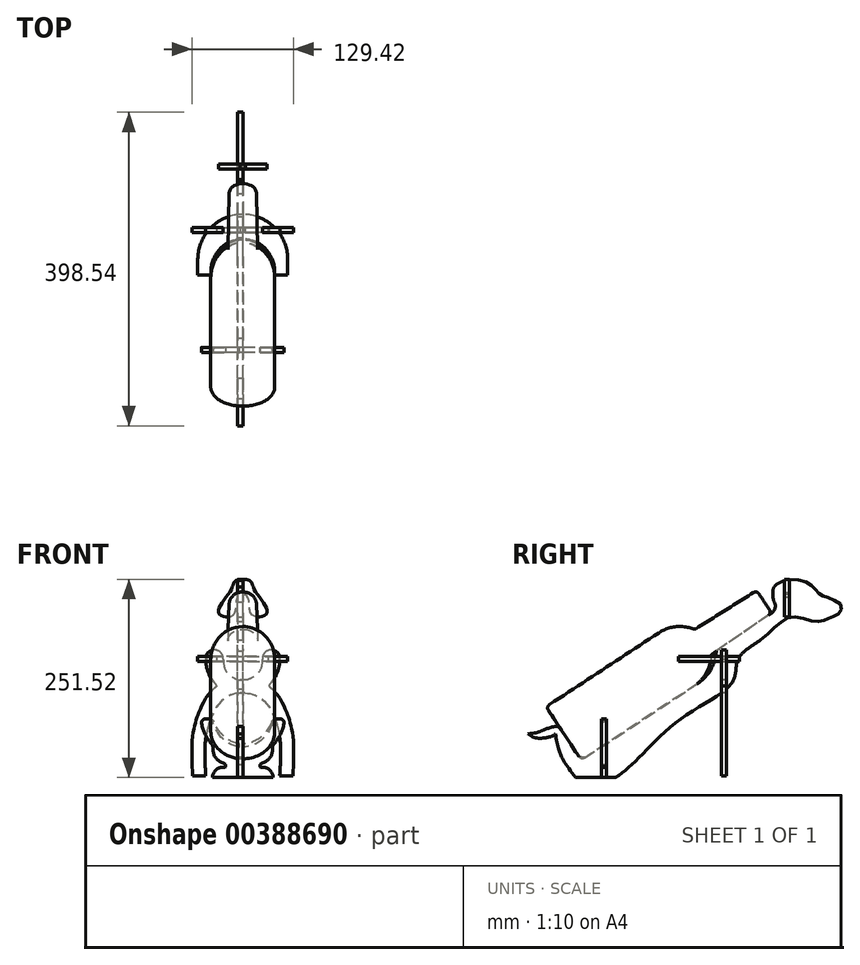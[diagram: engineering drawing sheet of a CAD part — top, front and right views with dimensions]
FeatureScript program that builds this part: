
annotation { "Feature Type Name" : "Feature", "Feature Type Description" : "" }
export const myFeature = defineFeature(function(context is Context, id is Id, definition is map)
    precondition{}
    {
        {
            var Q0;
            Q0=qCreatedBy(makeId("Right.planeOp"),FACE);
            var sketch = newSketch(context, id + "F0", { "sketchPlane" : qUnion([Q0])});
            skLineSegment(sketch, "E0", {"start": v(127.91, 114.02) * mm, "end": v(-126.79, -53.4) * mm});
            skLineSegment(sketch, "E1", {"start": v(-126.79, -53.4) * mm, "end": v(-107.26, -83.12) * mm});
            skLineSegment(sketch, "E2", {"start": v(16.48, 40.77) * mm, "end": v(38.8, 6.81) * mm, "construction": true});
            skLineSegment(sketch, "E3", {"start": v(50.09, 62.86) * mm, "end": v(60.55, 46.94) * mm, "construction": true});
            skLineSegment(sketch, "E4", {"start": v(127.91, 114.02) * mm, "end": v(134.6, 103.85) * mm});
            skLineSegment(sketch, "E5", {"start": v(38.8, 6.81) * mm, "end": v(-100.22, -84.57) * mm});
            skLineSegment(sketch, "E6", {"start": v(133.23, 96.87) * mm, "end": v(62.16, 48.05) * mm});
            skPoint(sketch, "E7.visualSharp", {"position": v(60.55, 46.94) * mm});
            skPoint(sketch, "E8.visualSharp", {"position": v(137.33, 99.7) * mm});
            skArc(sketch, "E8.filletArc", {"start": v(133.23, 96.87) * mm, "mid": v(135.34, 100.08) * mm, "end": v(134.6, 103.85) * mm});
            skPoint(sketch, "E9.visualSharp", {"position": v(-104.47, -87.36) * mm});
            skArc(sketch, "E9.filletArc", {"start": v(-107.26, -83.12) * mm, "mid": v(-104.04, -85.3) * mm, "end": v(-100.22, -84.57) * mm});
            skArc(sketch, "E10", {"start": v(38.8, 6.81) * mm, "mid": v(54.27, 23.32) * mm, "end": v(60.5, 45.07) * mm});
            skArc(sketch, "E11.filletArc", {"start": v(62.16, 48.05) * mm, "mid": v(60.98, 46.75) * mm, "end": v(60.5, 45.07) * mm});
            skSolve(sketch);
        }
        {
            var Q0;
            Q0=qCreatedBy(makeId("Right.planeOp"),FACE);
            var sketch = newSketch(context, id + "F1", { "sketchPlane" : qUnion([Q0])});
            skLineSegment(sketch, "E12", {"start": v(126.38, 106.7) * mm, "end": v(-128.33, -60.73) * mm});
            skLineSegment(sketch, "E13", {"start": v(-128.33, -60.73) * mm, "end": v(-108.8, -90.44) * mm});
            skLineSegment(sketch, "E14", {"start": v(14.94, 33.45) * mm, "end": v(37.27, -0.51) * mm, "construction": true});
            skLineSegment(sketch, "E15", {"start": v(48.55, 55.54) * mm, "end": v(59.01, 39.62) * mm, "construction": true});
            skLineSegment(sketch, "E16", {"start": v(126.38, 106.7) * mm, "end": v(133.06, 96.52) * mm});
            skLineSegment(sketch, "E17", {"start": v(37.27, -0.51) * mm, "end": v(-101.76, -91.9) * mm});
            skLineSegment(sketch, "E18", {"start": v(131.7, 89.55) * mm, "end": v(60.62, 40.72) * mm});
            skPoint(sketch, "E19.visualSharp", {"position": v(59.01, 39.62) * mm});
            skPoint(sketch, "E20.visualSharp", {"position": v(135.8, 92.37) * mm});
            skArc(sketch, "E20.filletArc", {"start": v(131.7, 89.55) * mm, "mid": v(133.8, 92.76) * mm, "end": v(133.06, 96.52) * mm});
            skPoint(sketch, "E21.visualSharp", {"position": v(-106, -94.69) * mm});
            skArc(sketch, "E21.filletArc", {"start": v(-108.8, -90.44) * mm, "mid": v(-105.58, -92.63) * mm, "end": v(-101.76, -91.9) * mm});
            skArc(sketch, "E22", {"start": v(37.27, -0.51) * mm, "mid": v(52.73, 16) * mm, "end": v(58.97, 37.74) * mm});
            skArc(sketch, "E23.filletArc", {"start": v(60.62, 40.72) * mm, "mid": v(59.44, 39.43) * mm, "end": v(58.97, 37.74) * mm});
            skLineSegment(sketch, "E24", {"start": v(150.96, 122.85) * mm, "end": v(-151.82, -76.17) * mm, "construction": true});
            skSolve(sketch);
        }
        {
            var Q0;
            Q0=makeQuery(id+"F1.imprint","IMPRINT",FACE,{"disambiguationData":[TD([[makeQuery(id+"F1.imprint","IMPRINT",EDGE,{"derivedFrom":sQuery(id+"F1.wireOp",EDGE,"E12")}),1.0]])]});
            var Q1;
            Q1=sQuery(id+"F1.wireOp",EDGE,"E24");
            revolve(context, id + "F2", {"entities" : qUnion([Q0]), "axis" : qUnion([Q1]), "revolveType" : RevolveType.FULL});
        }
        {
            var Q0;
            Q0=qCreatedBy(makeId("Right.planeOp"),FACE);
            cPlane(context, id + "F3", {"entities" : qUnion([Q0]), "cplaneType" : CPlaneType.OFFSET, "offset" : 1 / 203.2 * mm, "width" : 152.4 * mm, "height" : 152.4 * mm});
        }
        {
            var Q0;
            Q0=qCreatedBy(makeId("Right.planeOp"),FACE);
            var sketch = newSketch(context, id + "F4", { "sketchPlane" : qUnion([Q0])});
            skLineSegment(sketch, "E25", {"start": v(132.15, 111.22) * mm, "end": v(-122.55, -56.2) * mm});
            skLineSegment(sketch, "E26", {"start": v(-122.55, -56.2) * mm, "end": v(-103.02, -85.91) * mm});
            skLineSegment(sketch, "E27", {"start": v(20.72, 37.98) * mm, "end": v(43.04, 4.02) * mm, "construction": true});
            skLineSegment(sketch, "E28", {"start": v(54.33, 60.07) * mm, "end": v(64.8, 44.15) * mm, "construction": true});
            skLineSegment(sketch, "E29", {"start": v(132.15, 111.22) * mm, "end": v(138.84, 101.06) * mm});
            skLineSegment(sketch, "E30", {"start": v(43.04, 4.02) * mm, "end": v(-95.98, -87.37) * mm});
            skLineSegment(sketch, "E31", {"start": v(137.47, 94.08) * mm, "end": v(66.4, 45.25) * mm});
            skPoint(sketch, "E32.visualSharp", {"position": v(64.8, 44.15) * mm});
            skPoint(sketch, "E33.visualSharp", {"position": v(141.57, 96.9) * mm});
            skArc(sketch, "E33.filletArc", {"start": v(137.47, 94.08) * mm, "mid": v(139.58, 97.29) * mm, "end": v(138.84, 101.06) * mm});
            skPoint(sketch, "E34.visualSharp", {"position": v(-100.23, -90.16) * mm});
            skArc(sketch, "E34.filletArc", {"start": v(-103.02, -85.91) * mm, "mid": v(-99.8, -88.1) * mm, "end": v(-95.98, -87.37) * mm});
            skArc(sketch, "E35", {"start": v(43.04, 4.02) * mm, "mid": v(58.5, 20.53) * mm, "end": v(64.75, 42.27) * mm});
            skArc(sketch, "E36.filletArc", {"start": v(66.4, 45.25) * mm, "mid": v(65.22, 43.96) * mm, "end": v(64.75, 42.27) * mm});
            skLineSegment(sketch, "E37", {"start": v(156.74, 127.39) * mm, "end": v(-146.04, -71.64) * mm, "construction": true});
            skSolve(sketch);
        }
        {
            var Q0;
            Q0=qCreatedBy(id+"F3.planeOp",FACE);
            var sketch = newSketch(context, id + "F5", { "sketchPlane" : qUnion([Q0])});
            skLineSegment(sketch, "E38", {"start": v(129.3, 111.9) * mm, "end": v(-125.4, -55.52) * mm, "construction": true});
            skLineSegment(sketch, "E39", {"start": v(-125.4, -55.52) * mm, "end": v(-107.26, -83.12) * mm, "construction": true});
            skLineSegment(sketch, "E40", {"start": v(17.87, 38.65) * mm, "end": v(38.8, 6.82) * mm, "construction": true});
            skLineSegment(sketch, "E41", {"start": v(51.48, 60.74) * mm, "end": v(60.55, 46.95) * mm, "construction": true});
            skLineSegment(sketch, "E42", {"start": v(129.3, 111.9) * mm, "end": v(134.6, 103.86) * mm, "construction": true});
            skLineSegment(sketch, "E43", {"start": v(38.8, 6.82) * mm, "end": v(-100.22, -84.57) * mm, "construction": true});
            skLineSegment(sketch, "E44", {"start": v(133.23, 96.88) * mm, "end": v(62.15, 48.05) * mm, "construction": true});
            skPoint(sketch, "E45.visualSharp", {"position": v(60.55, 46.95) * mm});
            skPoint(sketch, "E46.visualSharp", {"position": v(137.33, 99.7) * mm});
            skArc(sketch, "E46.filletArc", {"start": v(133.23, 96.88) * mm, "mid": v(135.33, 100.09) * mm, "end": v(134.6, 103.86) * mm, "construction": true});
            skPoint(sketch, "E47.visualSharp", {"position": v(-104.47, -87.36) * mm});
            skArc(sketch, "E47.filletArc", {"start": v(-107.26, -83.12) * mm, "mid": v(-104.04, -85.3) * mm, "end": v(-100.22, -84.57) * mm, "construction": true});
            skArc(sketch, "E48", {"start": v(38.8, 6.82) * mm, "mid": v(54.27, 23.33) * mm, "end": v(60.5, 45.07) * mm, "construction": true});
            skArc(sketch, "E49.filletArc", {"start": v(62.15, 48.05) * mm, "mid": v(60.98, 46.76) * mm, "end": v(60.5, 45.07) * mm, "construction": true});
            skLineSegment(sketch, "E50.0", {"start": v(138.84, 106.65) * mm, "end": v(139.13, 106.2) * mm});
            skArc(sketch, "E50.1", {"start": v(136.1, 92.7) * mm, "mid": v(140.32, 99.11) * mm, "end": v(138.84, 106.65) * mm});
            skLineSegment(sketch, "E50.2", {"start": v(136.1, 92.7) * mm, "end": v(65.55, 44.22) * mm});
            skLineSegment(sketch, "E50.3", {"start": v(-129.48, -58.56) * mm, "end": v(-111.5, -85.9) * mm});
            skArc(sketch, "E50.4", {"start": v(-111.5, -85.9) * mm, "mid": v(-105.07, -90.28) * mm, "end": v(-97.43, -88.82) * mm});
            skLineSegment(sketch, "E50.5", {"start": v(41.6, 2.57) * mm, "end": v(-97.43, -88.82) * mm});
            skArc(sketch, "E50.6", {"start": v(41.6, 2.57) * mm, "mid": v(58.53, 20.54) * mm, "end": v(65.55, 44.22) * mm});
            skLineSegment(sketch, "E51", {"start": v(-113.23, -116.39) * mm, "end": v(-62.43, -116.39) * mm});
            skLineSegment(sketch, "E52", {"start": v(11, -17.54) * mm, "end": v(24.95, -38.77) * mm, "construction": true});
            skLineSegment(sketch, "E53", {"start": v(58.53, 20.54) * mm, "end": v(86.35, 5.26) * mm, "construction": true});
            skLineSegment(sketch, "E54", {"start": v(109.97, 74.74) * mm, "end": v(121.48, 57.99) * mm, "construction": true});
            skFitSpline(sketch, "E55", {"points": [v(-62.43, -116.39) * mm, v(-33.54, -92.29) * mm, v(24.95, -38.77) * mm, v(86.35, 5.26) * mm, v(93.72, 34.9) * mm, v(121.48, 57.99) * mm], "startDerivative": vector(159.16, 104.1) * mm, "endDerivative": vector(168.13, 123.76) * mm});
            skFitSpline(sketch, "E56", {"points": [v(121.48, 57.99) * mm, v(144.71, 78.58) * mm, v(164.56, 87.66) * mm, v(189.26, 81.98) * mm, v(202.82, 83.08) * mm, v(211.13, 87.06) * mm, v(220.95, 91.79) * mm, v(224.26, 101.6) * mm, v(210.78, 110.76) * mm, v(200, 114.83) * mm, v(193.5, 120.19) * mm, v(185.37, 128.25) * mm, v(165.8, 135.1) * mm, v(139.13, 125.69) * mm], "startDerivative": vector(256.26, 194.91) * mm, "endDerivative": vector(-141.62, -197.05) * mm});
            skLineSegment(sketch, "E57", {"start": v(-120.57, -72.1) * mm, "end": v(-134.37, -81.18) * mm, "construction": true});
            skFitSpline(sketch, "E58", {"points": [v(-113.23, -116.39) * mm, v(-130.64, -91.32) * mm, v(-134.37, -81.18) * mm, v(-138.76, -60.93) * mm], "startDerivative": vector(-50.46, 62) * mm, "endDerivative": vector(-7.82, 62.45) * mm});
            skFitSpline(sketch, "E59", {"points": [v(-138.76, -60.93) * mm, v(-147.9, -65.45) * mm, v(-173.85, -60.93) * mm], "startDerivative": vector(-24.4, -25.88) * mm, "endDerivative": vector(-40.71, 38.74) * mm});
            skFitSpline(sketch, "E60", {"points": [v(-173.85, -60.93) * mm, v(-153.82, -56.03) * mm, v(-135.34, -51.57) * mm], "startDerivative": vector(89.48, 8.4) * mm, "endDerivative": vector(32.86, -1.06) * mm});
            skLineSegment(sketch, "E61", {"start": v(-133.74, -53.46) * mm, "end": v(-129.84, -58.08) * mm});
            skArc(sketch, "E62.filletArc", {"start": v(-133.74, -53.46) * mm, "mid": v(-135.72, -52.03) * mm, "end": v(-138.13, -51.69) * mm});
            skPoint(sketch, "E63.visualSharp", {"position": v(-129.64, -58.3) * mm});
            skArc(sketch, "E63.filletArc", {"start": v(-129.48, -58.56) * mm, "mid": v(-129.65, -58.31) * mm, "end": v(-129.84, -58.08) * mm});
            skFitSpline(sketch, "E64", {"points": [v(139.13, 125.69) * mm, v(139.13, 106.2) * mm], "startDerivative": vector(-7.3, -7.68) * mm, "endDerivative": vector(7.6, -15.97) * mm});
            skSolve(sketch);
        }
        {
            var Q0;
            Q0 = qSketchRegion(id + "F5", true);
            extrude(context, id + "F6", {"entities" : qUnion([Q0]), "oppositeDirection" : true, "depth" : 6.35 * mm});
        }
        {
            var Q0;
            Q0=makeQuery(id+"F6.opExtrude","CAP_FACE",FACE,{"disambiguationData":[OSD([sQuery(id+"F5.wireOp",EDGE,"E50.0"),sQuery(id+"F5.wireOp",EDGE,"E50.1"),sQuery(id+"F5.wireOp",EDGE,"E50.2"),sQuery(id+"F5.wireOp",EDGE,"E50.3"),sQuery(id+"F5.wireOp",EDGE,"E50.4"),sQuery(id+"F5.wireOp",EDGE,"E50.5"),sQuery(id+"F5.wireOp",EDGE,"E50.6"),sQuery(id+"F5.wireOp",EDGE,"E51"),sQuery(id+"F5.wireOp",EDGE,"E55"),sQuery(id+"F5.wireOp",EDGE,"E56"),sQuery(id+"F5.wireOp",EDGE,"E58"),sQuery(id+"F5.wireOp",EDGE,"E59"),sQuery(id+"F5.wireOp",EDGE,"E60"),sQuery(id+"F5.wireOp",EDGE,"E61"),sQuery(id+"F5.wireOp",EDGE,"E62.filletArc"),sQuery(id+"F5.wireOp",EDGE,"E63.filletArc"),sQuery(id+"F5.wireOp",EDGE,"E64")])],"isStart":true});
            var sketch = newSketch(context, id + "F7", { "sketchPlane" : qUnion([Q0])});
            skLineSegment(sketch, "E65.bottom", {"start": v(158.54, 134.8) * mm, "end": v(152.2, 134.8) * mm});
            skLineSegment(sketch, "E65.top", {"start": v(158.54, 118.28) * mm, "end": v(152.2, 118.28) * mm});
            skLineSegment(sketch, "E65.left", {"start": v(158.54, 134.8) * mm, "end": v(158.54, 118.28) * mm});
            skLineSegment(sketch, "E65.right", {"start": v(152.2, 134.8) * mm, "end": v(152.2, 118.28) * mm});
            skLineSegment(sketch, "E66.bottom", {"start": v(71.86, -9.33) * mm, "end": v(78.21, -9.33) * mm});
            skLineSegment(sketch, "E66.top", {"start": v(71.86, 7.18) * mm, "end": v(78.21, 7.18) * mm});
            skLineSegment(sketch, "E66.left", {"start": v(71.86, -9.33) * mm, "end": v(71.86, 7.18) * mm});
            skLineSegment(sketch, "E66.right", {"start": v(78.21, -9.33) * mm, "end": v(78.21, 7.18) * mm});
            skLineSegment(sketch, "E67.bottom", {"start": v(94.97, 37) * mm, "end": v(78.46, 37) * mm});
            skLineSegment(sketch, "E67.top", {"start": v(94.97, 30.65) * mm, "end": v(78.46, 30.65) * mm});
            skLineSegment(sketch, "E67.left", {"start": v(94.97, 37) * mm, "end": v(94.97, 30.65) * mm});
            skLineSegment(sketch, "E67.right", {"start": v(78.46, 37) * mm, "end": v(78.46, 30.65) * mm});
            skLineSegment(sketch, "E68.bottom", {"start": v(-74.18, -116.39) * mm, "end": v(-80.53, -116.39) * mm});
            skLineSegment(sketch, "E68.top", {"start": v(-74.18, -99.88) * mm, "end": v(-80.53, -99.88) * mm});
            skLineSegment(sketch, "E68.left", {"start": v(-74.18, -116.39) * mm, "end": v(-74.18, -99.88) * mm});
            skLineSegment(sketch, "E68.right", {"start": v(-80.53, -116.39) * mm, "end": v(-80.53, -99.88) * mm});
            skSolve(sketch);
        }
        {
            var Q0;
            Q0 = qSketchRegion(id + "F7", true);
            extrude(context, id + "F8", {"entities" : qUnion([Q0]), "operationType" : NewBodyOperationType.REMOVE, "endBound" : BoundingType.UP_TO_NEXT, "oppositeDirection" : true, "depth" : 25.4 * mm});
        }
        {
            var Q0;
            Q0=makeQuery(id+"F8.boolean.opBoolean","COPY",FACE,{"derivedFrom":makeQuery(id+"F8.opExtrude","SWEPT_FACE",FACE,{"disambiguationData":[OSD([sQuery(id+"F7.wireOp",EDGE,"E68.right")])]})});
            cPlane(context, id + "F9", {"entities" : qUnion([Q0]), "cplaneType" : CPlaneType.OFFSET, "offset" : 0 * mm, "width" : 152.4 * mm, "height" : 152.4 * mm});
        }
        {
            var Q0;
            Q0=qCreatedBy(id+"F9.planeOp",FACE);
            var sketch = newSketch(context, id + "F10", { "sketchPlane" : qUnion([Q0])});
            skLineSegment(sketch, "E69", {"start": v(0, -40.19) * mm, "end": v(0, -116.39) * mm, "construction": true});
            skLineSegment(sketch, "E70", {"start": v(0, -76.17) * mm, "end": v(38.1, -76.17) * mm, "construction": true});
            skArc(sketch, "E71.0", {"start": v(39.63, -73.76) * mm, "mid": v(47.76, -61.8) * mm, "end": v(52.39, -48.11) * mm});
            skFitSpline(sketch, "E72", {"points": [v(38.45, -116.39) * mm, v(28.54, -104) * mm, v(21.75, -102.5) * mm], "startDerivative": vector(1.02, 30.03) * mm, "endDerivative": vector(-6.25, 15.83) * mm});
            skFitSpline(sketch, "E73", {"points": [v(21.75, -102.5) * mm, v(28.95, -96.1) * mm, v(36.72, -87.28) * mm, v(38.1, -75.4) * mm], "startDerivative": vector(-7.38, 35.84) * mm, "endDerivative": vector(2.11, 45.83) * mm});
            skArc(sketch, "E74.filletArc", {"start": v(39.63, -73.76) * mm, "mid": v(38.46, -75.63) * mm, "end": v(38, -77.79) * mm});
            skFitSpline(sketch, "E75.MirrorCS", {"points": [v(-38.45, -116.39) * mm, v(-28.54, -104) * mm, v(-21.75, -102.5) * mm], "startDerivative": vector(-1.02, 30.03) * mm, "endDerivative": vector(6.25, 15.83) * mm});
            skFitSpline(sketch, "E76.MirrorCS", {"points": [v(-21.75, -102.5) * mm, v(-28.95, -96.1) * mm, v(-36.72, -87.28) * mm, v(-38.1, -75.4) * mm], "startDerivative": vector(7.38, 35.84) * mm, "endDerivative": vector(-2.11, 45.83) * mm});
            skArc(sketch, "E77.MirrorCS", {"start": v(-39.63, -73.76) * mm, "mid": v(-47.76, -61.8) * mm, "end": v(-52.39, -48.11) * mm});
            skArc(sketch, "E78.MirrorCS", {"start": v(-39.63, -73.76) * mm, "mid": v(-38.46, -75.63) * mm, "end": v(-38, -77.79) * mm});
            skLineSegment(sketch, "E79.MirrorCS", {"start": v(0, -76.17) * mm, "end": v(-38.1, -76.17) * mm, "construction": true});
            skLineSegment(sketch, "E80", {"start": v(47.4, -42.07) * mm, "end": v(0, -42.07) * mm});
            skPoint(sketch, "E81.visualSharp", {"position": v(53.19, -42.07) * mm});
            skArc(sketch, "E81.filletArc", {"start": v(52.39, -48.11) * mm, "mid": v(51.31, -43.92) * mm, "end": v(47.4, -42.07) * mm});
            skPoint(sketch, "E82.MirrorP", {"position": v(-53.19, -42.07) * mm});
            skLineSegment(sketch, "E83.MirrorCS", {"start": v(-47.4, -42.07) * mm, "end": v(0, -42.07) * mm});
            skArc(sketch, "E84.MirrorCS", {"start": v(-52.39, -48.11) * mm, "mid": v(-51.31, -43.92) * mm, "end": v(-47.4, -42.07) * mm});
            skPoint(sketch, "E85.MirrorCS.start.orphan", {"position": v(-39.63, -73.76) * mm});
            skLineSegment(sketch, "E86", {"start": v(0, -116.39) * mm, "end": v(38.45, -116.39) * mm});
            skLineSegment(sketch, "E87.MirrorCS", {"start": v(0, -116.39) * mm, "end": v(-38.45, -116.39) * mm});
            skSolve(sketch);
        }
        {
            var Q0;
            Q0 = qSketchRegion(id + "F10", true);
            extrude(context, id + "F11", {"entities" : qUnion([Q0]), "depth" : 6.35 * mm});
        }
        {
            var Q0;
            Q0=makeQuery(id+"F8.boolean.opBoolean","COPY",FACE,{"derivedFrom":makeQuery(id+"F8.opExtrude","SWEPT_FACE",FACE,{"disambiguationData":[OSD([sQuery(id+"F7.wireOp",EDGE,"E67.top")])]})});
            var sketch = newSketch(context, id + "F12", { "sketchPlane" : qUnion([Q0])});
            skLineSegment(sketch, "E88", {"start": v(0, 92.08) * mm, "end": v(0, 60.86) * mm, "construction": true});
            skPoint(sketch, "E88.endSnap0", {"position": v(0, 78.46) * mm});
            skLineSegment(sketch, "E89", {"start": v(0, 37.82) * mm, "end": v(0, 94.97) * mm, "construction": true});
            skLineSegment(sketch, "E90", {"start": v(0, 60.86) * mm, "end": v(-16.24, 60.86) * mm, "construction": true});
            skLineSegment(sketch, "E91", {"start": v(0, 37.82) * mm, "end": v(-40.64, 37.82) * mm, "construction": true});
            skArc(sketch, "E92", {"start": v(0, 78.46) * mm, "mid": v(-28.74, 66.55) * mm, "end": v(-40.64, 37.82) * mm, "construction": true});
            skArc(sketch, "E93.0", {"start": v(0, 94.97) * mm, "mid": v(-40.41, 78.23) * mm, "end": v(-57.15, 37.82) * mm});
            skLineSegment(sketch, "E94", {"start": v(-40.64, 37.82) * mm, "end": v(-57.15, 37.82) * mm, "construction": true});
            skPoint(sketch, "E95.start.orphan", {"position": v(0, 105.65) * mm});
            skLineSegment(sketch, "E96.MirrorCS", {"start": v(0, 60.86) * mm, "end": v(16.24, 60.86) * mm, "construction": true});
            skLineSegment(sketch, "E97.MirrorCS", {"start": v(0, 37.82) * mm, "end": v(40.64, 37.82) * mm, "construction": true});
            skLineSegment(sketch, "E98.MirrorCS", {"start": v(40.64, 37.82) * mm, "end": v(57.15, 37.82) * mm, "construction": true});
            skArc(sketch, "E99.MirrorCS", {"start": v(0, 78.46) * mm, "mid": v(28.74, 66.55) * mm, "end": v(40.64, 37.82) * mm, "construction": true});
            skArc(sketch, "E100.MirrorCS", {"start": v(0, 94.97) * mm, "mid": v(40.41, 78.23) * mm, "end": v(57.15, 37.82) * mm});
            skLineSegment(sketch, "E101", {"start": v(57.15, 37.82) * mm, "end": v(57.15, 17.76) * mm});
            skLineSegment(sketch, "E102", {"start": v(40.64, 17.76) * mm, "end": v(40.64, 37.82) * mm, "construction": true});
            skLineSegment(sketch, "E103.MirrorCS", {"start": v(-57.15, 37.82) * mm, "end": v(-57.15, 17.76) * mm});
            skLineSegment(sketch, "E104.MirrorCS", {"start": v(-40.64, 17.76) * mm, "end": v(-40.64, 37.82) * mm, "construction": true});
            skLineSegment(sketch, "E105", {"start": v(57.15, 17.76) * mm, "end": v(-57.15, 17.76) * mm});
            skSolve(sketch);
        }
        {
            var Q0;
            Q0 = qSketchRegion(id + "F12", true);
            extrude(context, id + "F13", {"entities" : qUnion([Q0]), "depth" : 6.35 * mm});
        }
        {
            var Q0;
            Q0=makeQuery(id+"F8.boolean.opBoolean","COPY",FACE,{"derivedFrom":makeQuery(id+"F8.opExtrude","SWEPT_FACE",FACE,{"disambiguationData":[OSD([sQuery(id+"F7.wireOp",EDGE,"E66.left")])]})});
            var sketch = newSketch(context, id + "F14", { "sketchPlane" : qUnion([Q0])});
            skLineSegment(sketch, "E106", {"start": v(0, -9.33) * mm, "end": v(38.1, -9.33) * mm, "construction": true});
            skLineSegment(sketch, "E107", {"start": v(0, -9.33) * mm, "end": v(0, 49.4) * mm, "construction": true});
            skPoint(sketch, "E107.endSnap0", {"position": v(0, 7.18) * mm});
            skLineSegment(sketch, "E108", {"start": v(0, 28.02) * mm, "end": v(38.1, 28.02) * mm, "construction": true});
            skLineSegment(sketch, "E109", {"start": v(0, 34.37) * mm, "end": v(38.1, 34.37) * mm, "construction": true});
            skLineSegment(sketch, "E110", {"start": v(0, -114.37) * mm, "end": v(-47, -114.37) * mm, "construction": true});
            skFitSpline(sketch, "E111", {"points": [v(-3.17, -9.33) * mm, v(-40.9, -42.11) * mm, v(-47, -114.37) * mm], "startDerivative": vector(-141.52, -3.48) * mm, "endDerivative": vector(12.9, -201.55) * mm});
            skLineSegment(sketch, "E112", {"start": v(-3.17, -9.33) * mm, "end": v(0, -9.33) * mm});
            skArc(sketch, "E113", {"start": v(-47.2, 34.37) * mm, "mid": v(-43.8, 16.78) * mm, "end": v(-34.1, 1.72) * mm});
            skFitSpline(sketch, "E114", {"points": [v(-24.85, 34.37) * mm, v(-18.77, 15.57) * mm, v(-3.18, 7.18) * mm], "startDerivative": vector(2.66, -57.69) * mm, "endDerivative": vector(26.33, 0.45) * mm});
            skFitSpline(sketch, "E115.0", {"points": [v(-3.7, 9.85) * mm, v(-5.78, 9.79) * mm, v(-9.9, 9.42) * mm, v(-15.79, 8.2) * mm, v(-21.34, 6.3) * mm, v(-26.48, 3.85) * mm, v(-31.16, 0.92) * mm, v(-35.37, -2.38) * mm, v(-39.12, -5.97) * mm, v(-43.55, -11) * mm, v(-48.11, -17.62) * mm, v(-51.68, -24.32) * mm, v(-53.77, -28.94) * mm, v(-54.87, -31.55) * mm, v(-55.64, -33.47) * mm, v(-56.25, -35.06) * mm, v(-56.71, -36.3) * mm, v(-57.4, -38.18) * mm, v(-58.37, -41) * mm, v(-59.54, -44.8) * mm, v(-60.6, -48.63) * mm, v(-61.52, -52.52) * mm, v(-62.6, -57.79) * mm, v(-63.61, -64.57) * mm, v(-64.36, -73.13) * mm, v(-64.68, -82.26) * mm, v(-64.6, -95.46) * mm, v(-64.03, -106.84) * mm, v(-63.46, -115.4) * mm]});
            skLineSegment(sketch, "E116", {"start": v(-47, -114.37) * mm, "end": v(-63.53, -114.37) * mm});
            skLineSegment(sketch, "E117", {"start": v(-47.2, 34.37) * mm, "end": v(-24.85, 34.37) * mm, "construction": true});
            skLineSegment(sketch, "E118", {"start": v(-3.18, 7.18) * mm, "end": v(0, 7.18) * mm});
            skArc(sketch, "E119", {"start": v(-24.85, 34.37) * mm, "mid": v(-36.03, 45.54) * mm, "end": v(-47.2, 34.37) * mm});
            skPoint(sketch, "E120.visualSharp", {"position": v(-30.92, -1.3) * mm});
            skArc(sketch, "E120.filletArc", {"start": v(-34.47, -3.9) * mm, "mid": v(-33.04, -1.17) * mm, "end": v(-34.1, 1.72) * mm});
            skFitSpline(sketch, "E121.MirrorCS", {"points": [v(3.17, -9.33) * mm, v(40.9, -42.11) * mm, v(47, -114.37) * mm], "startDerivative": vector(141.52, -3.48) * mm, "endDerivative": vector(-12.9, -201.55) * mm});
            skArc(sketch, "E122.MirrorCS", {"start": v(47.2, 34.37) * mm, "mid": v(43.8, 16.78) * mm, "end": v(34.1, 1.72) * mm});
            skArc(sketch, "E123.MirrorCS", {"start": v(24.85, 34.37) * mm, "mid": v(36.03, 45.54) * mm, "end": v(47.2, 34.37) * mm});
            skFitSpline(sketch, "E124.MirrorCS", {"points": [v(24.85, 34.37) * mm, v(18.77, 15.57) * mm, v(3.17, 7.18) * mm], "startDerivative": vector(-2.66, -57.69) * mm, "endDerivative": vector(-26.33, 0.45) * mm});
            skLineSegment(sketch, "E125.MirrorCS", {"start": v(47, -114.37) * mm, "end": v(63.53, -114.37) * mm});
            skLineSegment(sketch, "E126.MirrorCS", {"start": v(3.17, -9.33) * mm, "end": v(0, -9.33) * mm});
            skLineSegment(sketch, "E127.MirrorCS", {"start": v(3.18, 7.18) * mm, "end": v(0, 7.18) * mm});
            skPoint(sketch, "E128.MirrorP", {"position": v(30.92, -1.3) * mm});
            skArc(sketch, "E129.MirrorCS", {"start": v(34.47, -3.9) * mm, "mid": v(33.04, -1.17) * mm, "end": v(34.1, 1.72) * mm});
            skFitSpline(sketch, "E130.trimOffspring", {"points": [v(3.7, 9.85) * mm, v(5.78, 9.79) * mm, v(9.9, 9.42) * mm, v(15.79, 8.2) * mm, v(21.34, 6.3) * mm, v(26.48, 3.85) * mm, v(31.16, 0.92) * mm, v(35.37, -2.38) * mm, v(39.12, -5.97) * mm, v(43.55, -11) * mm, v(48.11, -17.62) * mm, v(51.68, -24.32) * mm, v(53.77, -28.94) * mm, v(54.87, -31.55) * mm, v(55.64, -33.47) * mm, v(56.25, -35.06) * mm, v(56.71, -36.3) * mm, v(57.4, -38.18) * mm, v(58.37, -41) * mm, v(59.54, -44.8) * mm, v(60.6, -48.63) * mm, v(61.52, -52.52) * mm, v(62.6, -57.79) * mm, v(63.61, -64.57) * mm, v(64.36, -73.13) * mm, v(64.68, -82.26) * mm, v(64.6, -95.46) * mm, v(64.03, -106.84) * mm, v(63.46, -115.4) * mm]});
            skSolve(sketch);
        }
        {
            var Q0;
            Q0 = qSketchRegion(id + "F14", true);
            var Q1;
            Q1=makeQuery(id+"F14.imprint","IMPRINT",FACE,{"disambiguationData":[TD([[makeQuery(id+"F14.imprint","IMPRINT",EDGE,{"derivedFrom":sQuery(id+"F14.wireOp",EDGE,"E111")}),-1.0]])]});
            extrude(context, id + "F15", {"entities" : qUnion([Q0, Q1]), "depth" : 6.35 * mm});
        }
        {
            var Q0;
            Q0=makeQuery(id+"F8.boolean.opBoolean","COPY",FACE,{"derivedFrom":makeQuery(id+"F8.opExtrude","SWEPT_FACE",FACE,{"disambiguationData":[OSD([sQuery(id+"F7.wireOp",EDGE,"E65.right")])]})});
            var sketch = newSketch(context, id + "F16", { "sketchPlane" : qUnion([Q0])});
            skFitSpline(sketch, "E131", {"points": [v(-3.2, 135.14) * mm, v(-9.9, 132.96) * mm, v(-15.3, 121.2) * mm, v(-30.6, 92.3) * mm, v(-12.46, 89.5) * mm, v(-7.85, 107.31) * mm, v(-3.43, 116.08) * mm], "startDerivative": vector(-41.32, -0.75) * mm, "endDerivative": vector(28.6, 19.54) * mm});
            skLineSegment(sketch, "E132", {"start": v(0, 135.13) * mm, "end": v(-3.43, 135.13) * mm});
            skLineSegment(sketch, "E133", {"start": v(0, 116.08) * mm, "end": v(-3.43, 116.08) * mm});
            skLineSegment(sketch, "E134", {"start": v(0, 116.08) * mm, "end": v(0, 135.13) * mm, "construction": true});
            skLineSegment(sketch, "E135.MirrorCS", {"start": v(0, 116.08) * mm, "end": v(3.43, 116.08) * mm});
            skFitSpline(sketch, "E136.MirrorCS", {"points": [v(3.2, 135.14) * mm, v(9.9, 132.96) * mm, v(15.3, 121.2) * mm, v(30.6, 92.3) * mm, v(12.46, 89.5) * mm, v(7.85, 107.31) * mm, v(3.43, 116.08) * mm], "startDerivative": vector(41.32, -0.75) * mm, "endDerivative": vector(-28.6, 19.54) * mm});
            skLineSegment(sketch, "E137.MirrorCS", {"start": v(0, 135.13) * mm, "end": v(3.43, 135.13) * mm});
            skSolve(sketch);
        }
        {
            var Q0;
            Q0=makeQuery(id+"F2.opRevolve","SWEPT_BODY",BODY,{"disambiguationData":[OSD([sQuery(id+"F1.wireOp",EDGE,"E12"),sQuery(id+"F1.wireOp",EDGE,"E13"),sQuery(id+"F1.wireOp",EDGE,"E16"),sQuery(id+"F1.wireOp",EDGE,"E17"),sQuery(id+"F1.wireOp",EDGE,"E18"),sQuery(id+"F1.wireOp",EDGE,"E20.filletArc"),sQuery(id+"F1.wireOp",EDGE,"E21.filletArc"),sQuery(id+"F1.wireOp",EDGE,"E22"),sQuery(id+"F1.wireOp",EDGE,"E23.filletArc")])]});
            var Q1;
            Q1=makeQuery(id+"F11.opExtrude","SWEPT_BODY",BODY,{"disambiguationData":[OSD([sQuery(id+"F10.wireOp",EDGE,"E71.0"),sQuery(id+"F10.wireOp",EDGE,"E72"),sQuery(id+"F10.wireOp",EDGE,"E73"),sQuery(id+"F10.wireOp",EDGE,"i7DrPkE0-S8ub-x3QA-NO9s-Kfr4tVxiThyD"),sQuery(id+"F10.wireOp",EDGE,"E74.filletArc"),sQuery(id+"F10.wireOp",EDGE,"E78.MirrorCS"),sQuery(id+"F10.wireOp",EDGE,"E76.MirrorCS"),sQuery(id+"F10.wireOp",EDGE,"45cbf56c-de31-4f08-80e8-914a87e571a34.MirrorCS"),sQuery(id+"F10.wireOp",EDGE,"E75.MirrorCS"),sQuery(id+"F10.wireOp",EDGE,"E77.MirrorCS"),sQuery(id+"F10.wireOp",EDGE,"E80"),sQuery(id+"F10.wireOp",EDGE,"E81.filletArc"),sQuery(id+"F10.wireOp",EDGE,"E83.MirrorCS"),sQuery(id+"F10.wireOp",EDGE,"E84.MirrorCS")])]});
            booleanBodies(context, id + "F17", {"operationType" : BooleanOperationType.SUBTRACTION, "tools" : qUnion([Q0]), "targets" : qUnion([Q1]), "keepTools" : true});
        }
        {
            var Q0;
            Q0=makeQuery(id+"F17.opBoolean","INTERSECT",EDGE,{"disambiguationData":[OD(0.0)],"derivedFrom":[makeQuery(id+"F2.opRevolve","SWEPT_FACE",FACE,{"disambiguationData":[OSD([sQuery(id+"F1.wireOp",EDGE,"E17")])]}),makeQuery(id+"F11.opExtrude","SWEPT_FACE",FACE,{"disambiguationData":[OSD([sQuery(id+"F10.wireOp",EDGE,"E80"),sQuery(id+"F10.wireOp",EDGE,"E83.MirrorCS")])]})]});
            var Q1;
            Q1=makeQuery(id+"F17.opBoolean","INTERSECT",EDGE,{"disambiguationData":[OD(1.0)],"derivedFrom":[makeQuery(id+"F2.opRevolve","SWEPT_FACE",FACE,{"disambiguationData":[OSD([sQuery(id+"F1.wireOp",EDGE,"E17")])]}),makeQuery(id+"F11.opExtrude","SWEPT_FACE",FACE,{"disambiguationData":[OSD([sQuery(id+"F10.wireOp",EDGE,"E80"),sQuery(id+"F10.wireOp",EDGE,"E83.MirrorCS")])]})]});
            fillet(context, id + "F18", {"entities" : qUnion([Q0, Q1]), "radius" : 5.08 * mm, "tangentPropagation" : true, "allowEdgeOverflow" : false});
        }
        {
            var Q0;
            Q0=makeQuery(id+"F4.imprint","IMPRINT",FACE,{"disambiguationData":[TD([[makeQuery(id+"F4.imprint","IMPRINT",EDGE,{"derivedFrom":sQuery(id+"F4.wireOp",EDGE,"E25")}),1.0]])]});
            var Q1;
            Q1=sQuery(id+"F4.wireOp",EDGE,"E37");
            revolve(context, id + "F19", {"entities" : qUnion([Q0]), "axis" : qUnion([Q1]), "revolveType" : RevolveType.FULL});
        }
        {
            var Q0;
            Q0=makeQuery(id+"F19.opRevolve","SWEPT_BODY",BODY,{"disambiguationData":[OSD([sQuery(id+"F4.wireOp",EDGE,"E25"),sQuery(id+"F4.wireOp",EDGE,"E26"),sQuery(id+"F4.wireOp",EDGE,"E29"),sQuery(id+"F4.wireOp",EDGE,"E30"),sQuery(id+"F4.wireOp",EDGE,"E31"),sQuery(id+"F4.wireOp",EDGE,"E33.filletArc"),sQuery(id+"F4.wireOp",EDGE,"E34.filletArc"),sQuery(id+"F4.wireOp",EDGE,"E35"),sQuery(id+"F4.wireOp",EDGE,"E36.filletArc")])]});
            var Q1;
            Q1=makeQuery(id+"F13.opExtrude","SWEPT_BODY",BODY,{"disambiguationData":[OSD([sQuery(id+"F12.wireOp",EDGE,"E93.0"),sQuery(id+"F12.wireOp",EDGE,"E100.MirrorCS"),sQuery(id+"F12.wireOp",EDGE,"E101"),sQuery(id+"F12.wireOp",EDGE,"E103.MirrorCS"),sQuery(id+"F12.wireOp",EDGE,"E105")])]});
            booleanBodies(context, id + "F20", {"operationType" : BooleanOperationType.SUBTRACTION, "tools" : qUnion([Q0]), "targets" : qUnion([Q1])});
        }
        {
            var Q0;
            Q0=makeQuery(id+"F15.opExtrude","CAP_FACE",FACE,{"disambiguationData":[OSD([sQuery(id+"F14.wireOp",EDGE,"E111"),sQuery(id+"F14.wireOp",EDGE,"E113"),sQuery(id+"F14.wireOp",EDGE,"E114"),sQuery(id+"F14.wireOp",EDGE,"E115.0"),sQuery(id+"F14.wireOp",EDGE,"E116"),sQuery(id+"F14.wireOp",EDGE,"E119"),sQuery(id+"F14.wireOp",EDGE,"E118"),sQuery(id+"F14.wireOp",EDGE,"E112"),sQuery(id+"F14.wireOp",EDGE,"E120.filletArc"),sQuery(id+"F14.wireOp",EDGE,"E121.MirrorCS"),sQuery(id+"F14.wireOp",EDGE,"E123.MirrorCS"),sQuery(id+"F14.wireOp",EDGE,"E124.MirrorCS"),sQuery(id+"F14.wireOp",EDGE,"E125.MirrorCS"),sQuery(id+"F14.wireOp",EDGE,"E126.MirrorCS"),sQuery(id+"F14.wireOp",EDGE,"E127.MirrorCS"),sQuery(id+"F14.wireOp",EDGE,"E122.MirrorCS"),sQuery(id+"F14.wireOp",EDGE,"E129.MirrorCS"),sQuery(id+"F14.wireOp",EDGE,"E130.trimOffspring")])],"isStart":false});
            var sketch = newSketch(context, id + "F21", { "sketchPlane" : qUnion([Q0])});
            skLineSegment(sketch, "E138", {"start": v(24.62, 30.64) * mm, "end": v(32.88, 30.64) * mm, "construction": true});
            skLineSegment(sketch, "E139", {"start": v(24.62, 30.64) * mm, "end": v(24.62, 37) * mm, "construction": true});
            skLineSegment(sketch, "E140.bottom", {"start": v(32.88, 30.64) * mm, "end": v(24.62, 30.64) * mm});
            skLineSegment(sketch, "E140.top", {"start": v(32.88, 37) * mm, "end": v(24.62, 37) * mm});
            skLineSegment(sketch, "E140.left", {"start": v(32.88, 30.64) * mm, "end": v(32.88, 37) * mm});
            skLineSegment(sketch, "E140.right", {"start": v(24.62, 30.64) * mm, "end": v(24.62, 37) * mm});
            skLineSegment(sketch, "E141.MirrorCS", {"start": v(-24.62, 30.64) * mm, "end": v(-24.62, 37) * mm});
            skLineSegment(sketch, "E142.MirrorCS", {"start": v(-32.88, 30.64) * mm, "end": v(-24.62, 30.64) * mm});
            skLineSegment(sketch, "E143.MirrorCS", {"start": v(-24.62, 30.64) * mm, "end": v(-32.88, 30.64) * mm, "construction": true});
            skLineSegment(sketch, "E144.MirrorCS", {"start": v(-24.62, 30.64) * mm, "end": v(-24.62, 37) * mm, "construction": true});
            skLineSegment(sketch, "E145.MirrorCS", {"start": v(-32.88, 30.64) * mm, "end": v(-32.88, 37) * mm});
            skLineSegment(sketch, "E146.MirrorCS", {"start": v(-32.88, 37) * mm, "end": v(-24.62, 37) * mm});
            skSolve(sketch);
        }
        {
            var Q0;
            {var subQ3=sQuery(id+"F21.wireOp",EDGE,"E142.MirrorCS");Q0=makeQuery(id+"F21.imprint","IMPRINT",FACE,{"disambiguationData":[TD([[makeQuery(id+"F21.imprint","IMPRINT",EDGE,{"derivedFrom":subQ3}),1.0]])]});}
            var Q1;
            {var subQ6=sQuery(id+"F21.wireOp",EDGE,"E140.bottom");Q1=makeQuery(id+"F21.imprint","IMPRINT",FACE,{"disambiguationData":[TD([[makeQuery(id+"F21.imprint","IMPRINT",EDGE,{"derivedFrom":subQ6}),-1.0]])]});}
            extrude(context, id + "F22", {"entities" : qUnion([Q0, Q1]), "operationType" : NewBodyOperationType.REMOVE, "endBound" : BoundingType.UP_TO_NEXT, "oppositeDirection" : true, "depth" : 25.4 * mm});
        }
        {
            var Q0;
            Q0=makeQuery(id+"F15.opExtrude","SWEPT_BODY",BODY,{"disambiguationData":[OSD([sQuery(id+"F14.wireOp",EDGE,"E111"),sQuery(id+"F14.wireOp",EDGE,"E113"),sQuery(id+"F14.wireOp",EDGE,"E114"),sQuery(id+"F14.wireOp",EDGE,"E115.0"),sQuery(id+"F14.wireOp",EDGE,"E116"),sQuery(id+"F14.wireOp",EDGE,"E119"),sQuery(id+"F14.wireOp",EDGE,"E118"),sQuery(id+"F14.wireOp",EDGE,"E112"),sQuery(id+"F14.wireOp",EDGE,"E120.filletArc"),sQuery(id+"F14.wireOp",EDGE,"E121.MirrorCS"),sQuery(id+"F14.wireOp",EDGE,"E123.MirrorCS"),sQuery(id+"F14.wireOp",EDGE,"E124.MirrorCS"),sQuery(id+"F14.wireOp",EDGE,"E125.MirrorCS"),sQuery(id+"F14.wireOp",EDGE,"E126.MirrorCS"),sQuery(id+"F14.wireOp",EDGE,"E127.MirrorCS"),sQuery(id+"F14.wireOp",EDGE,"E122.MirrorCS"),sQuery(id+"F14.wireOp",EDGE,"E129.MirrorCS"),sQuery(id+"F14.wireOp",EDGE,"E130.trimOffspring")])]});
            var Q1;
            Q1=makeQuery(id+"F13.opExtrude","SWEPT_BODY",BODY,{"disambiguationData":[OSD([sQuery(id+"F12.wireOp",EDGE,"E93.0"),sQuery(id+"F12.wireOp",EDGE,"E100.MirrorCS"),sQuery(id+"F12.wireOp",EDGE,"E101"),sQuery(id+"F12.wireOp",EDGE,"E103.MirrorCS"),sQuery(id+"F12.wireOp",EDGE,"E105")])]});
            booleanBodies(context, id + "F23", {"operationType" : BooleanOperationType.SUBTRACTION, "tools" : qUnion([Q0]), "targets" : qUnion([Q1]), "keepTools" : true});
        }
        {
            var Q0;
            {var subQ7=sQuery(id+"F16.wireOp",EDGE,"E131");Q0=makeQuery(id+"F16.imprint","IMPRINT",FACE,{"disambiguationData":[TD([[makeQuery(id+"F16.imprint","IMPRINT",EDGE,{"derivedFrom":subQ7}),1.0]])]});}
            var Q1;
            {var subQ0=sQuery(id+"F7.wireOp",EDGE,"E65.right");var subQ8=makeQuery(id+"F8.boolean.opBoolean","COPY",EDGE,{"derivedFrom":makeQuery(id+"F8.opExtrude","CAP_EDGE",EDGE,{"disambiguationData":[OSD([subQ0])],"isStart":true})});Q1=makeQuery(id+"F16.imprint","IMPRINT",FACE,{"disambiguationData":[TD([[makeQuery(id+"F16.imprint","IMPRINT",EDGE,{"derivedFrom":subQ8}),1.0]])]});}
            extrude(context, id + "F24", {"entities" : qUnion([Q0, Q1]), "depth" : 6.35 * mm});
        }
        {
            var Q0;
            Q0=makeQuery(id+"F6.opExtrude","SWEPT_BODY",BODY,{"disambiguationData":[OSD([sQuery(id+"F5.wireOp",EDGE,"E50.0"),sQuery(id+"F5.wireOp",EDGE,"E50.1"),sQuery(id+"F5.wireOp",EDGE,"E50.2"),sQuery(id+"F5.wireOp",EDGE,"E50.3"),sQuery(id+"F5.wireOp",EDGE,"E50.4"),sQuery(id+"F5.wireOp",EDGE,"E50.5"),sQuery(id+"F5.wireOp",EDGE,"E50.6"),sQuery(id+"F5.wireOp",EDGE,"E51"),sQuery(id+"F5.wireOp",EDGE,"E55"),sQuery(id+"F5.wireOp",EDGE,"E56"),sQuery(id+"F5.wireOp",EDGE,"E58"),sQuery(id+"F5.wireOp",EDGE,"E59"),sQuery(id+"F5.wireOp",EDGE,"E60"),sQuery(id+"F5.wireOp",EDGE,"E61"),sQuery(id+"F5.wireOp",EDGE,"E62.filletArc"),sQuery(id+"F5.wireOp",EDGE,"E63.filletArc"),sQuery(id+"F5.wireOp",EDGE,"E64")])]});
            var Q1;
            Q1=makeQuery(id+"F24.opExtrude","SWEPT_BODY",BODY,{"disambiguationData":[OSD([sQuery(id+"F16.wireOp",EDGE,"E131"),sQuery(id+"F16.wireOp",EDGE,"E132"),sQuery(id+"F16.wireOp",EDGE,"E133"),sQuery(id+"F16.wireOp",EDGE,"E135.MirrorCS"),sQuery(id+"F16.wireOp",EDGE,"E136.MirrorCS"),sQuery(id+"F16.wireOp",EDGE,"E137.MirrorCS")])]});
            booleanBodies(context, id + "F25", {"operationType" : BooleanOperationType.SUBTRACTION, "tools" : qUnion([Q0]), "targets" : qUnion([Q1]), "keepTools" : true});
        }
        {
            var Q0;
            Q0=makeQuery(id+"F6.opExtrude","SWEPT_BODY",BODY,{"disambiguationData":[OSD([sQuery(id+"F5.wireOp",EDGE,"E50.0"),sQuery(id+"F5.wireOp",EDGE,"E50.1"),sQuery(id+"F5.wireOp",EDGE,"E50.2"),sQuery(id+"F5.wireOp",EDGE,"E50.3"),sQuery(id+"F5.wireOp",EDGE,"E50.4"),sQuery(id+"F5.wireOp",EDGE,"E50.5"),sQuery(id+"F5.wireOp",EDGE,"E50.6"),sQuery(id+"F5.wireOp",EDGE,"E51"),sQuery(id+"F5.wireOp",EDGE,"E55"),sQuery(id+"F5.wireOp",EDGE,"E56"),sQuery(id+"F5.wireOp",EDGE,"E58"),sQuery(id+"F5.wireOp",EDGE,"E59"),sQuery(id+"F5.wireOp",EDGE,"E60"),sQuery(id+"F5.wireOp",EDGE,"E61"),sQuery(id+"F5.wireOp",EDGE,"E62.filletArc"),sQuery(id+"F5.wireOp",EDGE,"E63.filletArc"),sQuery(id+"F5.wireOp",EDGE,"E64")])]});
            var Q1;
            Q1=makeQuery(id+"F13.opExtrude","SWEPT_BODY",BODY,{"disambiguationData":[OSD([sQuery(id+"F12.wireOp",EDGE,"E93.0"),sQuery(id+"F12.wireOp",EDGE,"E100.MirrorCS"),sQuery(id+"F12.wireOp",EDGE,"E101"),sQuery(id+"F12.wireOp",EDGE,"E103.MirrorCS"),sQuery(id+"F12.wireOp",EDGE,"E105")])]});
            booleanBodies(context, id + "F26", {"operationType" : BooleanOperationType.SUBTRACTION, "tools" : qUnion([Q0]), "targets" : qUnion([Q1]), "keepTools" : true});
        }
        {
            var Q0;
            Q0=makeQuery(id+"F6.opExtrude","SWEPT_BODY",BODY,{"disambiguationData":[OSD([sQuery(id+"F5.wireOp",EDGE,"E50.0"),sQuery(id+"F5.wireOp",EDGE,"E50.1"),sQuery(id+"F5.wireOp",EDGE,"E50.2"),sQuery(id+"F5.wireOp",EDGE,"E50.3"),sQuery(id+"F5.wireOp",EDGE,"E50.4"),sQuery(id+"F5.wireOp",EDGE,"E50.5"),sQuery(id+"F5.wireOp",EDGE,"E50.6"),sQuery(id+"F5.wireOp",EDGE,"E51"),sQuery(id+"F5.wireOp",EDGE,"E55"),sQuery(id+"F5.wireOp",EDGE,"E56"),sQuery(id+"F5.wireOp",EDGE,"E58"),sQuery(id+"F5.wireOp",EDGE,"E59"),sQuery(id+"F5.wireOp",EDGE,"E60"),sQuery(id+"F5.wireOp",EDGE,"E61"),sQuery(id+"F5.wireOp",EDGE,"E62.filletArc"),sQuery(id+"F5.wireOp",EDGE,"E63.filletArc"),sQuery(id+"F5.wireOp",EDGE,"E64")])]});
            var Q1;
            Q1=makeQuery(id+"F11.opExtrude","SWEPT_BODY",BODY,{"disambiguationData":[OSD([sQuery(id+"F10.wireOp",EDGE,"E71.0"),sQuery(id+"F10.wireOp",EDGE,"E72"),sQuery(id+"F10.wireOp",EDGE,"E73"),sQuery(id+"F10.wireOp",EDGE,"E74.filletArc"),sQuery(id+"F10.wireOp",EDGE,"E78.MirrorCS"),sQuery(id+"F10.wireOp",EDGE,"E76.MirrorCS"),sQuery(id+"F10.wireOp",EDGE,"E75.MirrorCS"),sQuery(id+"F10.wireOp",EDGE,"E77.MirrorCS"),sQuery(id+"F10.wireOp",EDGE,"E80"),sQuery(id+"F10.wireOp",EDGE,"E81.filletArc"),sQuery(id+"F10.wireOp",EDGE,"E83.MirrorCS"),sQuery(id+"F10.wireOp",EDGE,"E84.MirrorCS"),sQuery(id+"F10.wireOp",EDGE,"E86"),sQuery(id+"F10.wireOp",EDGE,"E87.MirrorCS")])]});
            booleanBodies(context, id + "F27", {"operationType" : BooleanOperationType.SUBTRACTION, "tools" : qUnion([Q0]), "targets" : qUnion([Q1]), "keepTools" : true});
        }
    });
